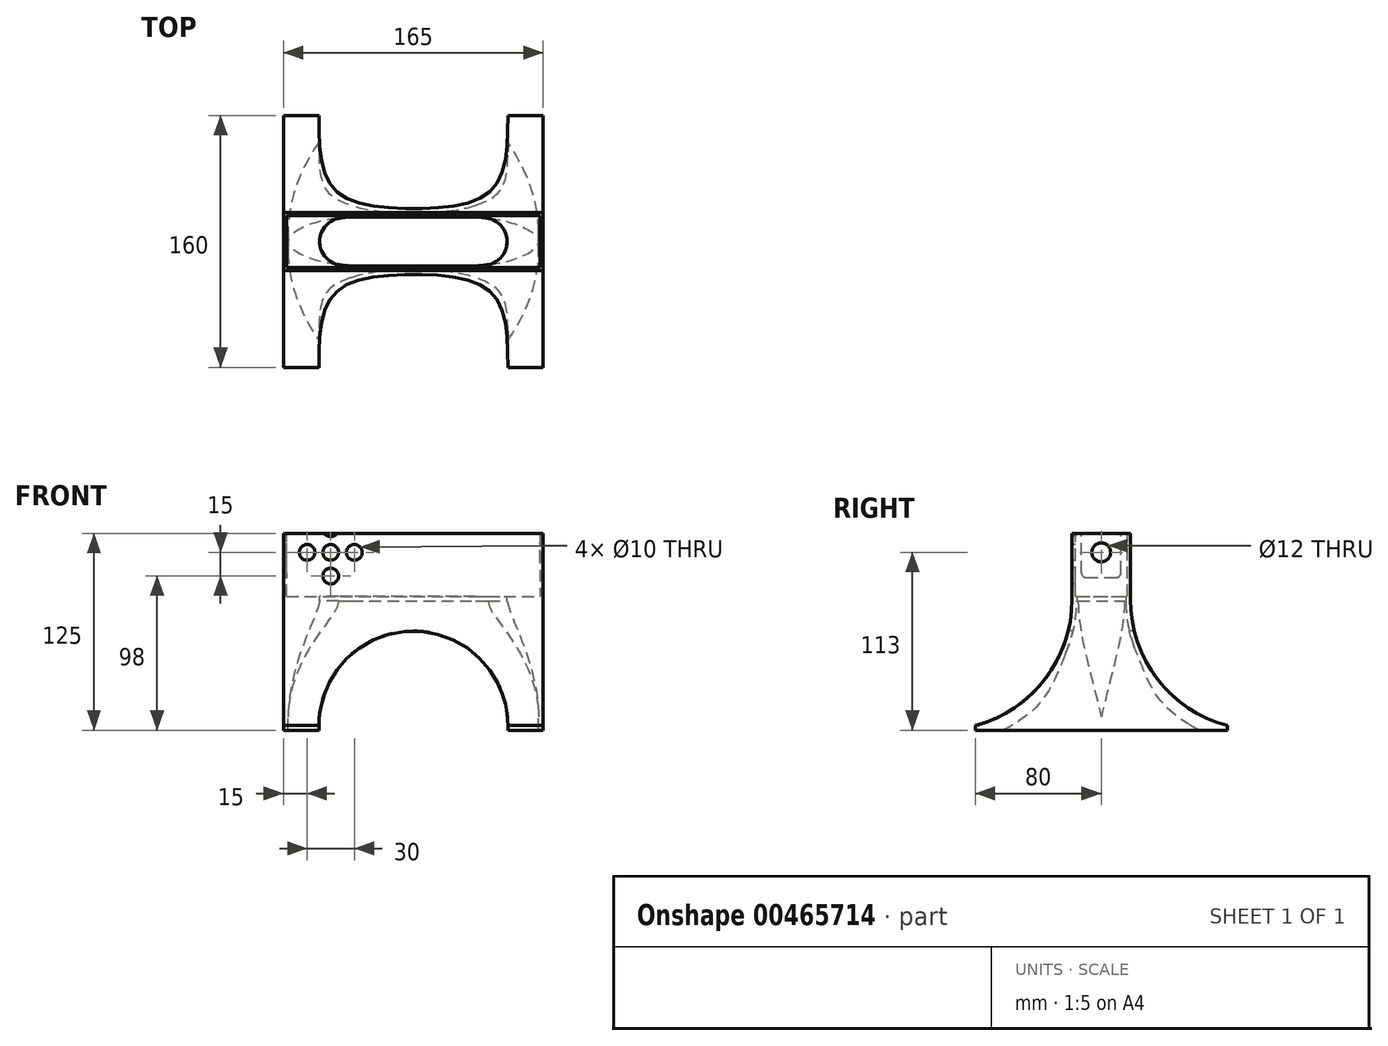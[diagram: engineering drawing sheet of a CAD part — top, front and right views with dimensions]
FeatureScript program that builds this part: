
annotation { "Feature Type Name" : "Feature", "Feature Type Description" : "" }
export const myFeature = defineFeature(function(context is Context, id is Id, definition is map)
    precondition{}
    {
        {
            var Q0;
            Q0=qCreatedBy(makeId("Front.planeOp"),FACE);
            var sketch = newSketch(context, id + "F0", { "sketchPlane" : qUnion([Q0])});
            skLineSegment(sketch, "E0.bottom", {"start": v(68.5, -20) * mm, "end": v(-68.5, -20) * mm});
            skLineSegment(sketch, "E0.top", {"start": v(80.5, 20) * mm, "end": v(-80.5, 20) * mm});
            skLineSegment(sketch, "E0.left", {"start": v(80.5, -8) * mm, "end": v(80.5, 20) * mm});
            skLineSegment(sketch, "E0.right", {"start": v(-80.5, -8) * mm, "end": v(-80.5, 20) * mm});
            skPoint(sketch, "E0.middle", {"position": v(0, 0) * mm});
            skPoint(sketch, "E1.visualSharp", {"position": v(-80.5, -20) * mm});
            skArc(sketch, "E1.filletArc", {"start": v(-80.5, -8) * mm, "mid": v(-76.99, -16.49) * mm, "end": v(-68.5, -20) * mm, "construction": true});
            skPoint(sketch, "E2.visualSharp", {"position": v(80.5, -20) * mm});
            skArc(sketch, "E2.filletArc", {"start": v(68.5, -20) * mm, "mid": v(76.99, -16.49) * mm, "end": v(80.5, -8) * mm, "construction": true});
            skLineSegment(sketch, "E3", {"start": v(-80.5, -8) * mm, "end": v(-80.5, -20) * mm});
            skLineSegment(sketch, "E4", {"start": v(-80.5, -20) * mm, "end": v(-68.5, -20) * mm});
            skLineSegment(sketch, "E5", {"start": v(80.5, -8) * mm, "end": v(80.5, -20) * mm});
            skLineSegment(sketch, "E6", {"start": v(80.5, -20) * mm, "end": v(68.5, -20) * mm});
            skSolve(sketch);
        }
        {
            var Q0;
            Q0 = qSketchRegion(id + "F0", true);
            extrude(context, id + "F1", {"entities" : qUnion([Q0]), "depth" : 33 * mm});
        }
        {
            var Q0;
            Q0=makeQuery(id+"F1.opExtrude","SWEPT_FACE",FACE,{"disambiguationData":[OSD([sQuery(id+"F0.wireOp",EDGE,"E0.bottom")])]});
            var sketch = newSketch(context, id + "F2", { "sketchPlane" : qUnion([Q0])});
            skLineSegment(sketch, "E7.bottom", {"start": v(56.5, 6) * mm, "end": v(-56.5, 6) * mm});
            skLineSegment(sketch, "E7.top", {"start": v(56.5, 27) * mm, "end": v(-56.5, 27) * mm});
            skLineSegment(sketch, "E7.left", {"start": v(56.5, 6) * mm, "end": v(56.5, 27) * mm});
            skLineSegment(sketch, "E7.right", {"start": v(-56.5, 6) * mm, "end": v(-56.5, 27) * mm});
            skPoint(sketch, "E7.middle", {"position": v(0, 16.5) * mm});
            skLineSegment(sketch, "E8", {"start": v(-80.5, 16.5) * mm, "end": v(80.5, 16.5) * mm, "construction": true});
            skSolve(sketch);
        }
        {
            var Q0;
            Q0 = qSketchRegion(id + "F2", true);
            extrude(context, id + "F3", {"entities" : qUnion([Q0]), "operationType" : NewBodyOperationType.REMOVE, "oppositeDirection" : true, "depth" : 2 * mm});
        }
        {
            var Q0;
            Q0=makeQuery(id+"F3.boolean.opBoolean","COPY",FACE,{"derivedFrom":makeQuery(id+"F3.opExtrude","CAP_FACE",FACE,{"disambiguationData":[OSD([sQuery(id+"F2.wireOp",EDGE,"E7.bottom"),sQuery(id+"F2.wireOp",EDGE,"E7.top"),sQuery(id+"F2.wireOp",EDGE,"E7.left"),sQuery(id+"F2.wireOp",EDGE,"E7.right")])],"isStart":false})});
            var Q1;
            Q1=makeQuery(id+"F1.opExtrude","SWEPT_FACE",FACE,{"disambiguationData":[OSD([sQuery(id+"F0.wireOp",EDGE,"E0.top")])]});
            var Q2;
            Q2=makeQuery(id+"F3.boolean.opBoolean","COPY",FACE,{"derivedFrom":makeQuery(id+"F3.opExtrude","SWEPT_FACE",FACE,{"disambiguationData":[OSD([sQuery(id+"F2.wireOp",EDGE,"E7.top")])]})});
            var Q3;
            Q3=makeQuery(id+"F3.boolean.opBoolean","COPY",FACE,{"derivedFrom":makeQuery(id+"F3.opExtrude","SWEPT_FACE",FACE,{"disambiguationData":[OSD([sQuery(id+"F2.wireOp",EDGE,"E7.right")])]})});
            var Q4;
            Q4=makeQuery(id+"F3.boolean.opBoolean","COPY",FACE,{"derivedFrom":makeQuery(id+"F3.opExtrude","SWEPT_FACE",FACE,{"disambiguationData":[OSD([sQuery(id+"F2.wireOp",EDGE,"E7.bottom")])]})});
            var Q5;
            Q5=makeQuery(id+"F3.boolean.opBoolean","COPY",FACE,{"derivedFrom":makeQuery(id+"F3.opExtrude","SWEPT_FACE",FACE,{"disambiguationData":[OSD([sQuery(id+"F2.wireOp",EDGE,"E7.left")])]})});
            var Q6;
            Q6=makeQuery(id+"F1.opExtrude","SWEPT_BODY",BODY,{"disambiguationData":[OSD([sQuery(id+"F0.wireOp",EDGE,"E0.bottom"),sQuery(id+"F0.wireOp",EDGE,"E0.top"),sQuery(id+"F0.wireOp",EDGE,"E0.left"),sQuery(id+"F0.wireOp",EDGE,"E0.right"),sQuery(id+"F0.wireOp",EDGE,"E1.filletArc"),sQuery(id+"F0.wireOp",EDGE,"E2.filletArc")])]});
            shell(context, id + "F4", {"entities" : qUnion([Q0, Q1, Q2, Q3, Q4, Q5]), "parts" : qUnion([Q6]), "thickness" : 2 * mm, "oppositeDirection" : true});
        }
        {
            var Q0;
            Q0=makeQuery(id+"F1.opExtrude","CAP_FACE",FACE,{"disambiguationData":[OSD([sQuery(id+"F0.wireOp",EDGE,"E0.bottom"),sQuery(id+"F0.wireOp",EDGE,"E0.top"),sQuery(id+"F0.wireOp",EDGE,"E0.left"),sQuery(id+"F0.wireOp",EDGE,"E0.right"),sQuery(id+"F0.wireOp",EDGE,"E1.filletArc"),sQuery(id+"F0.wireOp",EDGE,"E2.filletArc")])],"isStart":false});
            var sketch = newSketch(context, id + "F5", { "sketchPlane" : qUnion([Q0])});
            skCircle(sketch, "E9", {"center": v(-52.5, 8) * mm, "radius": 20 * mm, "construction": true});
            skCircle(sketch, "E10", {"center": v(-67.5, 8) * mm, "radius": 5 * mm});
            skPoint(sketch, "E10.first.point", {"position": v(-72.5, 8) * mm});
            skPoint(sketch, "E10.second.point", {"position": v(-62.5, 8.08) * mm});
            skPoint(sketch, "E10.third.point", {"position": v(-67.66, 3) * mm});
            skLineSegment(sketch, "E11", {"start": v(-72.5, 8) * mm, "end": v(-52.5, 8) * mm, "construction": true});
            skCircle(sketch, "E12.1.0", {"center": v(-52.5, -7) * mm, "radius": 5 * mm});
            skCircle(sketch, "E12.2.0", {"center": v(-37.5, 8) * mm, "radius": 5 * mm});
            skCircle(sketch, "E12.3.0", {"center": v(-52.5, 23) * mm, "radius": 5 * mm});
            skCircle(sketch, "E13", {"center": v(-52.5, 8) * mm, "radius": 5 * mm});
            skSolve(sketch);
        }
        {
            var Q0;
            Q0 = qSketchRegion(id + "F5", true);
            extrude(context, id + "F6", {"entities" : qUnion([Q0]), "operationType" : NewBodyOperationType.REMOVE, "oppositeDirection" : true, "depth" : 25 * mm});
        }
        {
            var Q0;
            Q0=makeQuery(id+"F1.opExtrude","SWEPT_FACE",FACE,{"disambiguationData":[OSD([sQuery(id+"F0.wireOp",EDGE,"E0.right")])]});
            var sketch = newSketch(context, id + "F7", { "sketchPlane" : qUnion([Q0])});
            skLineSegment(sketch, "E14.bottom", {"start": v(26, -8) * mm, "end": v(7, -8) * mm});
            skLineSegment(sketch, "E14.top", {"start": v(29, 48) * mm, "end": v(4, 48) * mm});
            skLineSegment(sketch, "E14.left", {"start": v(29, -5) * mm, "end": v(29, 48) * mm});
            skLineSegment(sketch, "E14.right", {"start": v(4, -5) * mm, "end": v(4, 48) * mm});
            skPoint(sketch, "E14.middle", {"position": v(16.5, 20) * mm});
            skPoint(sketch, "E15.visualSharp", {"position": v(29, -8) * mm});
            skArc(sketch, "E15.filletArc", {"start": v(26, -8) * mm, "mid": v(28.12, -7.12) * mm, "end": v(29, -5) * mm});
            skPoint(sketch, "E16.visualSharp", {"position": v(4, -8) * mm});
            skArc(sketch, "E16.filletArc", {"start": v(4, -5) * mm, "mid": v(4.88, -7.12) * mm, "end": v(7, -8) * mm});
            skSolve(sketch);
        }
        {
            var Q0;
            Q0 = qSketchRegion(id + "F7", true);
            extrude(context, id + "F8", {"entities" : qUnion([Q0]), "operationType" : NewBodyOperationType.REMOVE, "oppositeDirection" : true, "depth" : 25 * mm});
        }
        {
            var Q0;
            Q0=makeQuery(id+"F3.boolean.opBoolean","COPY",EDGE,{"derivedFrom":makeQuery(id+"F3.opExtrude","SWEPT_EDGE",EDGE,{"disambiguationData":[OSD([sQuery(id+"F2.wireOp",EDGE,"E7.top"),sQuery(id+"F2.wireOp",EDGE,"E7.left")])]})});
            var Q1;
            Q1=makeQuery(id+"F3.boolean.opBoolean","COPY",EDGE,{"derivedFrom":makeQuery(id+"F3.opExtrude","SWEPT_EDGE",EDGE,{"disambiguationData":[OSD([sQuery(id+"F2.wireOp",EDGE,"E7.bottom"),sQuery(id+"F2.wireOp",EDGE,"E7.left")])]})});
            var Q2;
            Q2=makeQuery(id+"F3.boolean.opBoolean","COPY",EDGE,{"derivedFrom":makeQuery(id+"F3.opExtrude","SWEPT_EDGE",EDGE,{"disambiguationData":[OSD([sQuery(id+"F2.wireOp",EDGE,"E7.top"),sQuery(id+"F2.wireOp",EDGE,"E7.right")])]})});
            var Q3;
            Q3=makeQuery(id+"F3.boolean.opBoolean","COPY",EDGE,{"derivedFrom":makeQuery(id+"F3.opExtrude","SWEPT_EDGE",EDGE,{"disambiguationData":[OSD([sQuery(id+"F2.wireOp",EDGE,"E7.bottom"),sQuery(id+"F2.wireOp",EDGE,"E7.right")])]})});
            fillet(context, id + "F9", {"entities" : qUnion([Q0, Q1, Q2, Q3]), "radius" : 5 * mm, "tangentPropagation" : true, "allowEdgeOverflow" : false});
        }
        {
            var Q0;
            Q0=makeQuery(id+"F1.opExtrude","SWEPT_FACE",FACE,{"disambiguationData":[OSD([sQuery(id+"F0.wireOp",EDGE,"E0.left")])]});
            var sketch = newSketch(context, id + "F10", { "sketchPlane" : qUnion([Q0])});
            skCircle(sketch, "E17", {"center": v(-16.5, 8) * mm, "radius": 6 * mm});
            skPoint(sketch, "E17.centerSnap0", {"position": v(-16.5, 20) * mm});
            skSolve(sketch);
        }
        {
            var Q0;
            Q0 = qSketchRegion(id + "F10", true);
            extrude(context, id + "F11", {"entities" : qUnion([Q0]), "operationType" : NewBodyOperationType.REMOVE, "oppositeDirection" : true, "depth" : 25 * mm});
        }
        {
            var Q0;
            Q0=makeQuery(id+"F1.opExtrude","SWEPT_FACE",FACE,{"disambiguationData":[OSD([sQuery(id+"F0.wireOp",EDGE,"E0.left"),sQuery(id+"F0.wireOp",EDGE,"E5")])]});
            var sketch = newSketch(context, id + "F12", { "sketchPlane" : qUnion([Q0])});
            skLineSegment(sketch, "E18", {"start": v(-227.35, -102) * mm, "end": v(194.35, -102) * mm, "construction": true});
            skLineSegment(sketch, "E19", {"start": v(-16.5, 8) * mm, "end": v(-16.5, -102) * mm, "construction": true});
            skArc(sketch, "E20", {"start": v(-96.5, -102) * mm, "mid": v(-52.15, -72.45) * mm, "end": v(-35, -22) * mm});
            skLineSegment(sketch, "E21", {"start": v(-96.5, -102) * mm, "end": v(-96.5, -105) * mm});
            skLineSegment(sketch, "E22", {"start": v(-96.5, -105) * mm, "end": v(-16.5, -105) * mm});
            skArc(sketch, "E23.MirrorCS", {"start": v(63.5, -102) * mm, "mid": v(19.15, -72.45) * mm, "end": v(2, -22) * mm});
            skLineSegment(sketch, "E24.MirrorCS", {"start": v(63.5, -105) * mm, "end": v(-16.5, -105) * mm});
            skLineSegment(sketch, "E25.MirrorCS", {"start": v(63.5, -102) * mm, "end": v(63.5, -105) * mm});
            skLineSegment(sketch, "E26", {"start": v(-35, -22) * mm, "end": v(2, -22) * mm});
            skSolve(sketch);
        }
        {
            var Q0;
            Q0 = qSketchRegion(id + "F12", true);
            var Q1;
            Q1=makeQuery(id+"F1.opExtrude","SWEPT_FACE",FACE,{"disambiguationData":[OSD([sQuery(id+"F0.wireOp",EDGE,"E0.right"),sQuery(id+"F0.wireOp",EDGE,"E3")])]});
            extrude(context, id + "F13", {"entities" : qUnion([Q0]), "operationType" : NewBodyOperationType.ADD, "endBound" : BoundingType.UP_TO_SURFACE, "oppositeDirection" : true, "endBoundEntityFace" : qUnion([Q1]), "depth" : 25 * mm});
        }
        {
            var Q0;
            Q0=makeQuery(id+"F13.opExtrude","SWEPT_FACE",FACE,{"disambiguationData":[OSD([sQuery(id+"F12.wireOp",EDGE,"E22"),sQuery(id+"F12.wireOp",EDGE,"E24.MirrorCS")])]});
            var Q1;
            Q1=makeQuery(id+"F13.opExtrude","SWEPT_FACE",FACE,{"disambiguationData":[OSD([sQuery(id+"F12.wireOp",EDGE,"E26")])]});
            shell(context, id + "F14", {"entities" : qUnion([Q0, Q1]), "thickness" : 3 * mm});
        }
        {
            var Q0;
            Q0=makeQuery(id+"F13.opExtrude","SWEPT_FACE",FACE,{"disambiguationData":[OSD([sQuery(id+"F12.wireOp",EDGE,"E26")])]});
            extrude(context, id + "F15", {"entities" : qUnion([Q0]), "operationType" : NewBodyOperationType.REMOVE, "oppositeDirection" : true, "depth" : 25 * mm});
        }
        {
            var Q0;
            Q0=makeQuery(id+"F14.opShell","OFFSET_EDGE",EDGE,{"disambiguationData":[OSD([sQuery(id+"F0.wireOp",EDGE,"E0.right"),sQuery(id+"F0.wireOp",EDGE,"E3"),sQuery(id+"F12.wireOp",EDGE,"E23.MirrorCS")])]});
            var Q1;
            Q1=makeQuery(id+"F14.opShell","OFFSET_EDGE",EDGE,{"disambiguationData":[OSD([sQuery(id+"F0.wireOp",EDGE,"E0.right"),sQuery(id+"F0.wireOp",EDGE,"E3"),sQuery(id+"F12.wireOp",EDGE,"E20")])]});
            var Q2;
            Q2=makeQuery(id+"F14.opShell","OFFSET_EDGE",EDGE,{"disambiguationData":[OSD([sQuery(id+"F12.wireOp",EDGE,"E23.MirrorCS")])]});
            var Q3;
            Q3=makeQuery(id+"F14.opShell","OFFSET_EDGE",EDGE,{"disambiguationData":[OSD([sQuery(id+"F12.wireOp",EDGE,"E20")])]});
            fillet(context, id + "F16", {"entities" : qUnion([Q0, Q1, Q2, Q3]), "radius" : 40 * mm, "tangentPropagation" : true, "allowEdgeOverflow" : false});
        }
        {
            var Q0;
            Q0=makeQuery(id+"F16.opFillet","BLEND_EDGE",EDGE,{"blendedFrom":[makeQuery(id+"F14.opShell","OFFSET_EDGE",EDGE,{"disambiguationData":[OSD([sQuery(id+"F12.wireOp",EDGE,"E20")])]}),makeQuery(id+"F14.opShell","OFFSET_EDGE",EDGE,{"disambiguationData":[OSD([sQuery(id+"F12.wireOp",EDGE,"E23.MirrorCS")])]})],"blendedInto":[]});
            var Q1;
            {var subQ0=sQuery(id+"F0.wireOp",EDGE,"E3");var subQ1=sQuery(id+"F0.wireOp",EDGE,"E0.right");Q1=makeQuery(id+"F16.opFillet","BLEND_EDGE",EDGE,{"blendedFrom":[makeQuery(id+"F14.opShell","OFFSET_EDGE",EDGE,{"disambiguationData":[OSD([subQ1,subQ0,sQuery(id+"F12.wireOp",EDGE,"E20")])]}),makeQuery(id+"F14.opShell","OFFSET_EDGE",EDGE,{"disambiguationData":[OSD([subQ1,subQ0,sQuery(id+"F12.wireOp",EDGE,"E23.MirrorCS")])]})],"blendedInto":[]});}
            fillet(context, id + "F17", {"entities" : qUnion([Q0, Q1]), "radius" : 15 * mm, "tangentPropagation" : true, "allowEdgeOverflow" : false});
        }
        {
            var Q0;
            Q0=makeQuery(id+"F14.opShell","OFFSET_FACE",FACE,{"disambiguationData":[OSD([sQuery(id+"F0.wireOp",EDGE,"E0.bottom"),sQuery(id+"F0.wireOp",EDGE,"E4"),sQuery(id+"F0.wireOp",EDGE,"E6")])]});
            extrude(context, id + "F18", {"entities" : qUnion([Q0]), "operationType" : NewBodyOperationType.REMOVE, "oppositeDirection" : true, "depth" : 25 * mm});
        }
        {
            var Q0;
            Q0=qCreatedBy(makeId("Front.planeOp"),FACE);
            var sketch = newSketch(context, id + "F19", { "sketchPlane" : qUnion([Q0])});
            skArc(sketch, "E27", {"start": v(60, -102) * mm, "mid": v(0, -42) * mm, "end": v(-60, -102) * mm});
            skLineSegment(sketch, "E28", {"start": v(0, -22) * mm, "end": v(0, -42) * mm, "construction": true});
            skPoint(sketch, "E28.endSnap0", {"position": v(0, -42) * mm});
            skLineSegment(sketch, "E29", {"start": v(-60, -102) * mm, "end": v(-60, -105) * mm});
            skLineSegment(sketch, "E30", {"start": v(-60, -105) * mm, "end": v(60, -105) * mm});
            skLineSegment(sketch, "E31", {"start": v(60, -105) * mm, "end": v(60, -102) * mm});
            skSolve(sketch);
        }
        {
            var Q0;
            Q0 = qSketchRegion(id + "F19", true);
            extrude(context, id + "F20", {"entities" : qUnion([Q0]), "operationType" : NewBodyOperationType.REMOVE, "endBound" : BoundingType.THROUGH_ALL, "oppositeDirection" : true, "depth" : 25 * mm, "hasSecondDirection" : true, "secondDirectionBound" : BoundingType.THROUGH_ALL, "secondDirectionOppositeDirection" : false, "secondDirectionDepth" : 25 * mm});
        }
    });
